# Revit family: Door-Exterior-Simpson-Traditional_Shaker
name_source: partatom
category: Doors
revit_build: Autodesk Revit Architecture 2012 (Build: 20110916_2132(x64)
units: mm (PartAtom-declared; Revit-internal decimal feet)

## types (1)
- Door-Exterior-Simpson-Traditional_Shaker
    Assembly Code = B2020100
    Bottom Rail Height = 9 3/16"
    Default Sill Height = 0"
    Description = Door
    Frame = Wood - Simpson Doors - Douglas Fir
    Frame Width = 3"
    Function = Exterior
    Height = 84"
    Lock Rail Height = 7 3/8"
    Lower Panel Height = 36"
    Manufacturer = Simpson Door Company
    Model = 000
    Number of Horizontal Divides = 4
    Panel = Wood - Simpson Doors - Douglas Fir
    Panel Stile Width = 4 7/16"
    Panel Thickness = 3/4"
    Panel Type = Traditional Shaker-Panel_w_Divides : Panel
    Product Documentation Link = http://www.simpsondoor.com
    Product Page URL = http://www.simpsondoor.com
    Rough Height = 81"
    Rough Width = 30"
    Show Bottom Vertical Divide = No
    Show Full Vertical Divide = No
    Show Split Vertical Divide = No
    Thickness = 1 3/4"
    Top Rail Height = 4 5/16"
    Top Secondary Panel Height = 8 1/2"
    Typical Horizontal Divide Width = 4"
    URL = http://www.simpsondoor.com
    UltraBlock Note = This Door Comes with The Option of UltraBlock Technology. It is Turn On as a Default
    UltraBlock Option = Yes
    Upper Horizontal Divide Width = 4"
    Vertical Divide Width = 4 3/8"
    Wall Closure = Exterior
    WaterBarrier Note = This Door Comes with The Option of WaterBarrier with UltraBlock Technology. It is Turn Off as a Default
    WaterBarrier with UltraBlock Technology = No
    Width = 36"
    Wood Species = http://simpsondoor.com
    Wood Species Note = Available in Any Wood Species

## geometry (parser evidence)
native form markers: Blend x24, Sweep x25
no freeform markers — native parametric forms only
